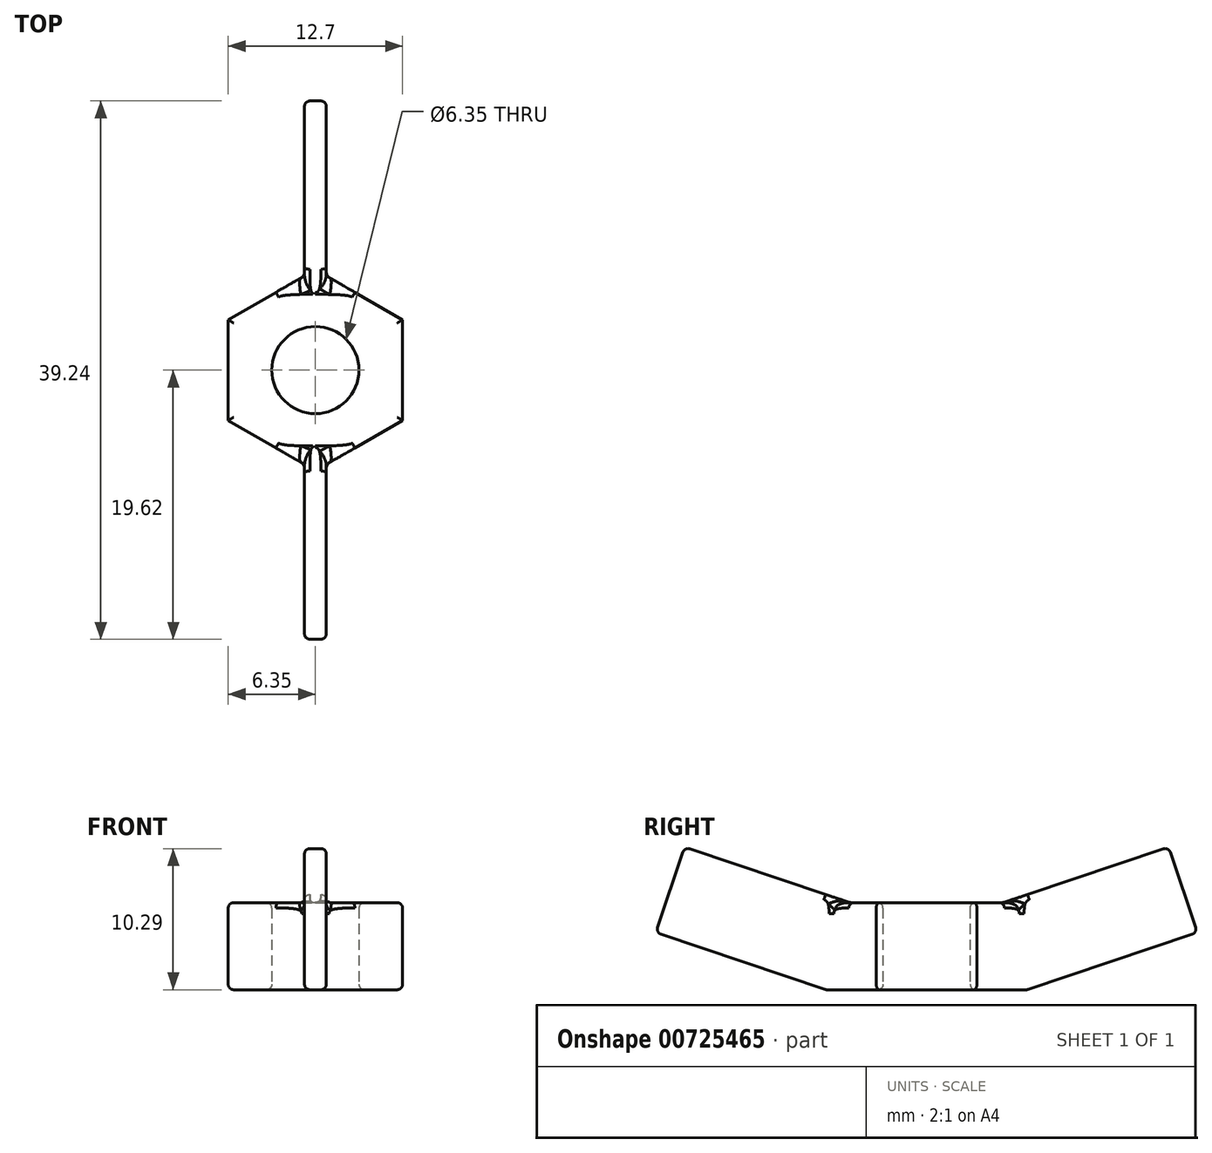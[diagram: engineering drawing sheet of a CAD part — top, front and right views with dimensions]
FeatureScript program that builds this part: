
annotation { "Feature Type Name" : "Feature", "Feature Type Description" : "" }
export const myFeature = defineFeature(function(context is Context, id is Id, definition is map)
    precondition{}
    {
        {
            var Q0;
            Q0=qCreatedBy(makeId("Top.planeOp"),FACE);
            var sketch = newSketch(context, id + "F0", { "sketchPlane" : qUnion([Q0])});
            skCircle(sketch, "E0", {"center": v(0, 0) * mm, "radius": 3.18 * mm});
            skCircle(sketch, "E1.cCircle", {"center": v(0, 0) * mm, "radius": 6.35 * mm, "construction": true});
            skLineSegment(sketch, "E1.0", {"start": v(6.35, 3.67) * mm, "end": v(6.35, -3.67) * mm});
            skLineSegment(sketch, "E1.1", {"start": v(6.35, -3.67) * mm, "end": v(0, -7.33) * mm});
            skLineSegment(sketch, "E1.2", {"start": v(0, -7.33) * mm, "end": v(-6.35, -3.67) * mm});
            skLineSegment(sketch, "E1.3", {"start": v(-6.35, -3.67) * mm, "end": v(-6.35, 3.67) * mm});
            skLineSegment(sketch, "E1.4", {"start": v(-6.35, 3.67) * mm, "end": v(0, 7.33) * mm});
            skLineSegment(sketch, "E1.5", {"start": v(0, 7.33) * mm, "end": v(6.35, 3.67) * mm});
            skPoint(sketch, "E1.0.midPoint", {"position": v(6.35, 0) * mm});
            skSolve(sketch);
        }
        {
            var Q0;
            Q0=makeQuery(id+"F0.imprint","IMPRINT",FACE,{"disambiguationData":[TD([[makeQuery(id+"F0.imprint","IMPRINT",EDGE,{"derivedFrom":sQuery(id+"F0.wireOp",EDGE,"E0")}),-1.0]])]});
            extrude(context, id + "F1", {"entities" : qUnion([Q0]), "depth" : 6.35 * mm, "offsetDistance" : 25.4 * mm});
        }
        {
            var Q0;
            Q0=qCreatedBy(makeId("Right.planeOp"),FACE);
            var sketch = newSketch(context, id + "F2", { "sketchPlane" : qUnion([Q0])});
            skLineSegment(sketch, "E2", {"start": v(-7.33, 0) * mm, "end": v(-19.72, 4.16) * mm});
            skLineSegment(sketch, "E3", {"start": v(-19.72, 4.16) * mm, "end": v(-17.63, 10.4) * mm});
            skLineSegment(sketch, "E4", {"start": v(-17.63, 10.4) * mm, "end": v(-5.59, 6.35) * mm});
            skLineSegment(sketch, "E5", {"start": v(-7.33, 6.35) * mm, "end": v(-5.59, 6.35) * mm});
            skLineSegment(sketch, "E6", {"start": v(-7.33, 0) * mm, "end": v(-5.59, 0) * mm});
            skLineSegment(sketch, "E7", {"start": v(-5.59, 0) * mm, "end": v(-5.59, 6.35) * mm});
            skLineSegment(sketch, "E8.MirrorCS", {"start": v(7.33, 0) * mm, "end": v(19.72, 4.16) * mm});
            skLineSegment(sketch, "E9.MirrorCS", {"start": v(19.72, 4.16) * mm, "end": v(17.63, 10.4) * mm});
            skLineSegment(sketch, "E10.MirrorCS", {"start": v(7.33, 0) * mm, "end": v(5.59, 0) * mm});
            skLineSegment(sketch, "E11.MirrorCS", {"start": v(17.63, 10.4) * mm, "end": v(5.59, 6.35) * mm});
            skLineSegment(sketch, "E12.MirrorCS", {"start": v(7.33, 6.35) * mm, "end": v(5.59, 6.35) * mm});
            skLineSegment(sketch, "E13.MirrorCS", {"start": v(5.59, 0) * mm, "end": v(5.59, 6.35) * mm});
            skSolve(sketch);
        }
        {
            var Q0;
            Q0 = qSketchRegion(id + "F2", true);
            extrude(context, id + "F3", {"entities" : qUnion([Q0]), "operationType" : NewBodyOperationType.ADD, "endBound" : BoundingType.SYMMETRIC, "depth" : 1.59 * mm, "offsetDistance" : 25.4 * mm});
        }
        {
            var Q0;
            Q0=makeQuery(id+"F3.opExtrude","CAP_FACE",FACE,{"disambiguationData":[OSD([sQuery(id+"F2.wireOp",EDGE,"E8.MirrorCS"),sQuery(id+"F2.wireOp",EDGE,"E9.MirrorCS"),sQuery(id+"F2.wireOp",EDGE,"E10.MirrorCS"),sQuery(id+"F2.wireOp",EDGE,"E11.MirrorCS"),sQuery(id+"F2.wireOp",EDGE,"E13.MirrorCS")])],"isStart":true});
            var Q1;
            Q1=makeQuery(id+"F3.opExtrude","CAP_FACE",FACE,{"disambiguationData":[OSD([sQuery(id+"F2.wireOp",EDGE,"E2"),sQuery(id+"F2.wireOp",EDGE,"E3"),sQuery(id+"F2.wireOp",EDGE,"E4"),sQuery(id+"F2.wireOp",EDGE,"E6"),sQuery(id+"F2.wireOp",EDGE,"E7")])],"isStart":true});
            var Q2;
            Q2=makeQuery(id+"F1.opExtrude","CAP_FACE",FACE,{"disambiguationData":[OSD([sQuery(id+"F0.wireOp",EDGE,"E0"),sQuery(id+"F0.wireOp",EDGE,"E1.0"),sQuery(id+"F0.wireOp",EDGE,"E1.1"),sQuery(id+"F0.wireOp",EDGE,"E1.2"),sQuery(id+"F0.wireOp",EDGE,"E1.3"),sQuery(id+"F0.wireOp",EDGE,"E1.4"),sQuery(id+"F0.wireOp",EDGE,"E1.5")])],"isStart":false});
            var Q3;
            Q3=makeQuery(id+"F3.opExtrude","CAP_FACE",FACE,{"disambiguationData":[OSD([sQuery(id+"F2.wireOp",EDGE,"E8.MirrorCS"),sQuery(id+"F2.wireOp",EDGE,"E9.MirrorCS"),sQuery(id+"F2.wireOp",EDGE,"E10.MirrorCS"),sQuery(id+"F2.wireOp",EDGE,"E11.MirrorCS"),sQuery(id+"F2.wireOp",EDGE,"E13.MirrorCS")])],"isStart":false});
            var Q4;
            Q4=makeQuery(id+"F3.opExtrude","CAP_FACE",FACE,{"disambiguationData":[OSD([sQuery(id+"F2.wireOp",EDGE,"E2"),sQuery(id+"F2.wireOp",EDGE,"E3"),sQuery(id+"F2.wireOp",EDGE,"E4"),sQuery(id+"F2.wireOp",EDGE,"E6"),sQuery(id+"F2.wireOp",EDGE,"E7")])],"isStart":false});
            var Q5;
            Q5=makeQuery(id+"F3.boolean.opBoolean","MERGE",FACE,{"derivedFrom":[makeQuery(id+"F1.opExtrude","CAP_FACE",FACE,{"disambiguationData":[OSD([sQuery(id+"F0.wireOp",EDGE,"E0"),sQuery(id+"F0.wireOp",EDGE,"E1.0"),sQuery(id+"F0.wireOp",EDGE,"E1.1"),sQuery(id+"F0.wireOp",EDGE,"E1.2"),sQuery(id+"F0.wireOp",EDGE,"E1.3"),sQuery(id+"F0.wireOp",EDGE,"E1.4"),sQuery(id+"F0.wireOp",EDGE,"E1.5")])],"isStart":true}),makeQuery(id+"F3.opExtrude","SWEPT_FACE",FACE,{"disambiguationData":[OSD([sQuery(id+"F2.wireOp",EDGE,"E6")])]}),makeQuery(id+"F3.opExtrude","SWEPT_FACE",FACE,{"disambiguationData":[OSD([sQuery(id+"F2.wireOp",EDGE,"E10.MirrorCS")])]})]});
            var Q6;
            Q6=makeQuery(id+"F3.opExtrude","SWEPT_EDGE",EDGE,{"disambiguationData":[OSD([sQuery(id+"F2.wireOp",EDGE,"E9.MirrorCS"),sQuery(id+"F2.wireOp",EDGE,"E11.MirrorCS")])]});
            var Q7;
            Q7=makeQuery(id+"F3.opExtrude","SWEPT_EDGE",EDGE,{"disambiguationData":[OSD([sQuery(id+"F2.wireOp",EDGE,"E8.MirrorCS"),sQuery(id+"F2.wireOp",EDGE,"E9.MirrorCS")])]});
            var Q8;
            Q8=makeQuery(id+"F3.opExtrude","SWEPT_FACE",FACE,{"disambiguationData":[OSD([sQuery(id+"F2.wireOp",EDGE,"E3")])]});
            fillet(context, id + "F4", {"entities" : qUnion([Q0, Q1, Q2, Q3, Q4, Q5, Q6, Q7, Q8]), "radius" : 0.4 * mm, "tangentPropagation" : true, "allowEdgeOverflow" : false});
        }
    });
